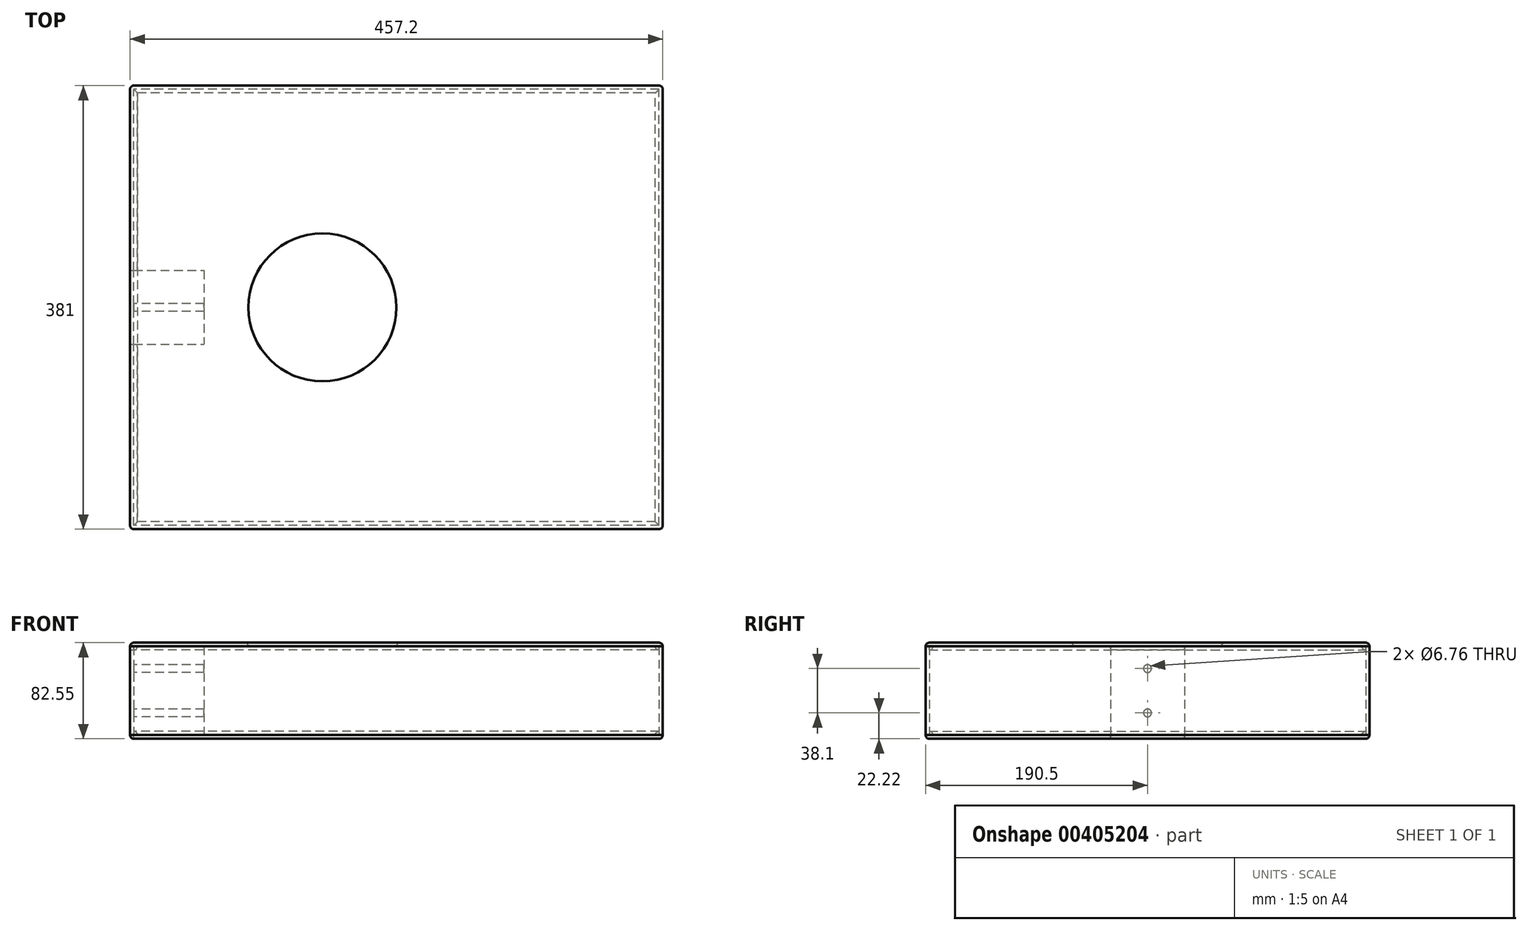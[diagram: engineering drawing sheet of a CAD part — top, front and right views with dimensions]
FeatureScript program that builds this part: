
annotation { "Feature Type Name" : "Feature", "Feature Type Description" : "" }
export const myFeature = defineFeature(function(context is Context, id is Id, definition is map)
    precondition{}
    {
        {
            var Q0;
            Q0=qCreatedBy(makeId("Top.planeOp"),FACE);
            var sketch = newSketch(context, id + "F0", { "sketchPlane" : qUnion([Q0])});
            skLineSegment(sketch, "E0.bottom", {"start": v(228.6, -190.5) * mm, "end": v(-228.6, -190.5) * mm});
            skLineSegment(sketch, "E0.top", {"start": v(228.6, 190.5) * mm, "end": v(-228.6, 190.5) * mm});
            skLineSegment(sketch, "E0.left", {"start": v(228.6, -190.5) * mm, "end": v(228.6, 190.5) * mm});
            skLineSegment(sketch, "E0.right", {"start": v(-228.6, -190.5) * mm, "end": v(-228.6, 190.5) * mm});
            skPoint(sketch, "E0.middle", {"position": v(0, 0) * mm});
            skLineSegment(sketch, "E1", {"start": v(-228.6, 0) * mm, "end": v(228.6, 0) * mm, "construction": true});
            skLineSegment(sketch, "E2.bottom", {"start": v(-228.6, 31.75) * mm, "end": v(-165.1, 31.75) * mm});
            skLineSegment(sketch, "E2.top", {"start": v(-228.6, -31.75) * mm, "end": v(-165.1, -31.75) * mm});
            skLineSegment(sketch, "E2.left", {"start": v(-228.6, 31.75) * mm, "end": v(-228.6, -31.75) * mm});
            skLineSegment(sketch, "E2.right", {"start": v(-165.1, 31.75) * mm, "end": v(-165.1, -31.75) * mm});
            skLineSegment(sketch, "E3.0", {"start": v(225.43, 187.33) * mm, "end": v(-225.43, 187.32) * mm});
            skLineSegment(sketch, "E3.1", {"start": v(225.43, -187.32) * mm, "end": v(225.42, 187.32) * mm});
            skLineSegment(sketch, "E3.2", {"start": v(225.43, -187.32) * mm, "end": v(-225.43, -187.33) * mm});
            skLineSegment(sketch, "E3.3", {"start": v(-225.42, -187.32) * mm, "end": v(-225.43, -31.75) * mm});
            skLineSegment(sketch, "E4.trimOffspring", {"start": v(-225.43, 31.75) * mm, "end": v(-225.43, 187.32) * mm});
            skLineSegment(sketch, "E5", {"start": v(-225.42, 187.32) * mm, "end": v(225.42, -187.32) * mm, "construction": true});
            skLineSegment(sketch, "E6", {"start": v(225.43, 187.33) * mm, "end": v(-225.43, -187.33) * mm, "construction": true});
            skLineSegment(sketch, "E7", {"start": v(-225.43, 109.54) * mm, "end": v(225.43, 109.54) * mm, "construction": true});
            skLineSegment(sketch, "E8", {"start": v(-225.42, -109.54) * mm, "end": v(225.42, -109.54) * mm, "construction": true});
            skLineSegment(sketch, "E9.0", {"start": v(-222.25, 31.75) * mm, "end": v(-222.25, 184.15) * mm});
            skLineSegment(sketch, "E9.1", {"start": v(-222.25, -184.15) * mm, "end": v(-222.25, -31.75) * mm});
            skLineSegment(sketch, "E9.2", {"start": v(222.25, -184.15) * mm, "end": v(-222.25, -184.15) * mm});
            skLineSegment(sketch, "E9.3", {"start": v(222.25, -184.15) * mm, "end": v(222.25, 184.15) * mm});
            skLineSegment(sketch, "E9.4", {"start": v(222.25, 184.15) * mm, "end": v(-222.25, 184.15) * mm});
            skLineSegment(sketch, "E10", {"start": v(-225.43, -31.75) * mm, "end": v(-225.43, 31.75) * mm});
            skSolve(sketch);
        }
        {
            var Q0;
            {var subQ9=sQuery(id+"F0.wireOp",EDGE,"E0.bottom");Q0=makeQuery(id+"F0.imprint","IMPRINT",FACE,{"disambiguationData":[TD([[makeQuery(id+"F0.imprint","IMPRINT",EDGE,{"derivedFrom":subQ9}),-1.0]])]});}
            var Q1;
            {var subQ0=sQuery(id+"F0.wireOp",EDGE,"E2.left");Q1=makeQuery(id+"F0.imprint","IMPRINT",FACE,{"disambiguationData":[TD([[makeQuery(id+"F0.imprint","IMPRINT",EDGE,{"derivedFrom":subQ0}),1.0]])]});}
            extrude(context, id + "F1", {"entities" : qUnion([Q0, Q1]), "depth" : 76.2 * mm});
        }
        {
            var Q0;
            Q0=makeQuery(id+"F0.imprint","IMPRINT",FACE,{"disambiguationData":[TD([[makeQuery(id+"F0.imprint","IMPRINT",EDGE,{"derivedFrom":sQuery(id+"F0.wireOp",EDGE,"E3.0")}),1.0]])]});
            extrude(context, id + "F2", {"entities" : qUnion([Q0]), "depth" : 3.17 * mm});
        }
        {
            var Q0;
            {var subQ0=sQuery(id+"F0.wireOp",EDGE,"E2.right");Q0=makeQuery(id+"F0.imprint","IMPRINT",FACE,{"disambiguationData":[TD([[makeQuery(id+"F0.imprint","IMPRINT",EDGE,{"derivedFrom":subQ0}),-1.0]])]});}
            extrude(context, id + "F3", {"entities" : qUnion([Q0]), "depth" : 76.2 * mm});
        }
        {
            var Q0;
            {var subQ22=sQuery(id+"F0.wireOp",EDGE,"E2.right");Q0=makeQuery(id+"F0.imprint","IMPRINT",FACE,{"disambiguationData":[TD([[makeQuery(id+"F0.imprint","IMPRINT",EDGE,{"derivedFrom":subQ22}),1.0]])]});}
            var Q1;
            {var subQ9=sQuery(id+"F0.wireOp",EDGE,"E0.bottom");Q1=makeQuery(id+"F0.imprint","IMPRINT",FACE,{"disambiguationData":[TD([[makeQuery(id+"F0.imprint","IMPRINT",EDGE,{"derivedFrom":subQ9}),-1.0]])]});}
            var Q2;
            Q2=makeQuery(id+"F0.imprint","IMPRINT",FACE,{"disambiguationData":[TD([[makeQuery(id+"F0.imprint","IMPRINT",EDGE,{"derivedFrom":sQuery(id+"F0.wireOp",EDGE,"E3.0")}),1.0]])]});
            var Q3;
            {var subQ3=sQuery(id+"F0.wireOp",EDGE,"9cd653e2-5831-4ef2-81ab-d4589cb25bf60.MirrorCS");var subQ5=sQuery(id+"F0.wireOp",EDGE,"FzasoPsy-j5LI-SKMa-pJql-VMQi0rBRJnUh");var subQ7=makeQuery(id+"F0.imprint","INTERSECT",VERTEX,{"derivedFrom":[subQ5,subQ3,sQuery(id+"F0.wireOp",EDGE,"aZBs2FEg-NMFi-UrqN-aLSZ-2lPHPGAGJXjl")]});Q3=makeQuery(id+"F0.imprint","IMPRINT",FACE,{"disambiguationData":[TD([[makeQuery(id+"F0.imprint","IMPRINT",EDGE,{"disambiguationData":[TD([[subQ7,-1.0]])],"derivedFrom":subQ5}),1.0]])]});}
            var Q4;
            {var subQ3=sQuery(id+"F0.wireOp",EDGE,"266a0d68-b8df-42f1-9db3-1c0c4b850da00.MirrorCS");var subQ5=sQuery(id+"F0.wireOp",EDGE,"953ce75e-d67b-4efc-bb00-0bf9153aae580.MirrorCS");var subQ6=makeQuery(id+"F0.imprint","INTERSECT",VERTEX,{"derivedFrom":[subQ5,subQ3]});Q4=makeQuery(id+"F0.imprint","IMPRINT",FACE,{"disambiguationData":[TD([[makeQuery(id+"F0.imprint","IMPRINT",EDGE,{"disambiguationData":[TD([[subQ6,-1.0]])],"derivedFrom":subQ5}),-1.0]])]});}
            var Q5;
            {var subQ0=sQuery(id+"F0.wireOp",EDGE,"htOpjW4I-LsWA-SOcr-SaNu-1bdWkilzWaC8");Q5=makeQuery(id+"F0.imprint","IMPRINT",FACE,{"disambiguationData":[TD([[makeQuery(id+"F0.imprint","IMPRINT",EDGE,{"derivedFrom":subQ0}),1.0]])]});}
            var Q6;
            {var subQ0=sQuery(id+"F0.wireOp",EDGE,"Kqx6j9Af-swEe-v3Xz-Lvxc-ByTmGhM5A1qr");Q6=makeQuery(id+"F0.imprint","IMPRINT",FACE,{"disambiguationData":[TD([[makeQuery(id+"F0.imprint","IMPRINT",EDGE,{"derivedFrom":subQ0}),-1.0]])]});}
            var Q7;
            {var subQ0=sQuery(id+"F0.wireOp",EDGE,"BsV5Qlrn-ofVC-NWyB-0alZ-GxZEvTZdQiUt");Q7=makeQuery(id+"F0.imprint","IMPRINT",FACE,{"disambiguationData":[TD([[makeQuery(id+"F0.imprint","IMPRINT",EDGE,{"derivedFrom":subQ0}),1.0]])]});}
            var Q8;
            {var subQ0=sQuery(id+"F0.wireOp",EDGE,"MGyNNtHl-DI8I-UvPv-GyAB-l8y68qR5pJX8");Q8=makeQuery(id+"F0.imprint","IMPRINT",FACE,{"disambiguationData":[TD([[makeQuery(id+"F0.imprint","IMPRINT",EDGE,{"derivedFrom":subQ0}),1.0]])]});}
            var Q9;
            {var subQ3=sQuery(id+"F0.wireOp",EDGE,"Kqx6j9Af-swEe-v3Xz-Lvxc-ByTmGhM5A1qr");Q9=makeQuery(id+"F0.imprint","IMPRINT",FACE,{"disambiguationData":[TD([[makeQuery(id+"F0.imprint","IMPRINT",EDGE,{"derivedFrom":subQ3}),1.0]])]});}
            var Q10;
            {var subQ2=sQuery(id+"F0.wireOp",EDGE,"2eb42779-513d-4441-a8d7-d657dc6821a70.MirrorCS");Q10=makeQuery(id+"F0.imprint","IMPRINT",FACE,{"disambiguationData":[TD([[makeQuery(id+"F0.imprint","IMPRINT",EDGE,{"derivedFrom":subQ2}),-1.0]])]});}
            var Q11;
            {var subQ0=sQuery(id+"F0.wireOp",EDGE,"953ce75e-d67b-4efc-bb00-0bf9153aae580.MirrorCS");var subQ1=sQuery(id+"F0.wireOp",EDGE,"9e805463-2b13-41b5-8116-62ebd402cd080.MirrorCS");var subQ2=makeQuery(id+"F0.imprint","INTERSECT",VERTEX,{"derivedFrom":[subQ1,subQ0]});Q11=makeQuery(id+"F0.imprint","IMPRINT",FACE,{"disambiguationData":[TD([[makeQuery(id+"F0.imprint","IMPRINT",EDGE,{"disambiguationData":[TD([[subQ2,1.0]])],"derivedFrom":subQ0}),-1.0]])]});}
            var Q12;
            {var subQ0=sQuery(id+"F0.wireOp",EDGE,"GMDVnvmZ-OlzJ-OGz9-7dtt-hA1VzcQCeQrP");var subQ1=sQuery(id+"F0.wireOp",EDGE,"1a1ql4DQ-ibnV-jcih-jIlv-f0bGRyVOqIzY");var subQ2=makeQuery(id+"F0.imprint","INTERSECT",VERTEX,{"derivedFrom":[subQ1,subQ0]});Q12=makeQuery(id+"F0.imprint","IMPRINT",FACE,{"disambiguationData":[TD([[makeQuery(id+"F0.imprint","IMPRINT",EDGE,{"disambiguationData":[TD([[subQ2,-1.0]])],"derivedFrom":subQ0}),1.0]])]});}
            var Q13;
            {var subQ0=sQuery(id+"F0.wireOp",EDGE,"953ce75e-d67b-4efc-bb00-0bf9153aae580.MirrorCS");var subQ1=sQuery(id+"F0.wireOp",EDGE,"9cd653e2-5831-4ef2-81ab-d4589cb25bf60.MirrorCS");var subQ2=makeQuery(id+"F0.imprint","INTERSECT",VERTEX,{"derivedFrom":[subQ1,subQ0]});Q13=makeQuery(id+"F0.imprint","IMPRINT",FACE,{"disambiguationData":[TD([[makeQuery(id+"F0.imprint","IMPRINT",EDGE,{"disambiguationData":[TD([[subQ2,-1.0]])],"derivedFrom":subQ0}),-1.0]])]});}
            var Q14;
            {var subQ0=sQuery(id+"F0.wireOp",EDGE,"FzasoPsy-j5LI-SKMa-pJql-VMQi0rBRJnUh");var subQ1=sQuery(id+"F0.wireOp",EDGE,"GMDVnvmZ-OlzJ-OGz9-7dtt-hA1VzcQCeQrP");var subQ2=makeQuery(id+"F0.imprint","INTERSECT",VERTEX,{"derivedFrom":[subQ1,subQ0]});Q14=makeQuery(id+"F0.imprint","IMPRINT",FACE,{"disambiguationData":[TD([[makeQuery(id+"F0.imprint","IMPRINT",EDGE,{"disambiguationData":[TD([[subQ2,1.0]])],"derivedFrom":subQ1}),1.0]])]});}
            var Q15;
            {var subQ0=sQuery(id+"F0.wireOp",EDGE,"E2.left");Q15=makeQuery(id+"F0.imprint","IMPRINT",FACE,{"disambiguationData":[TD([[makeQuery(id+"F0.imprint","IMPRINT",EDGE,{"derivedFrom":subQ0}),1.0]])]});}
            var Q16;
            Q16=makeQuery(id+"F0.imprint","IMPRINT",FACE,{"disambiguationData":[TD([[makeQuery(id+"F0.imprint","IMPRINT",EDGE,{"derivedFrom":sQuery(id+"F0.wireOp",EDGE,"4894fb85-a18e-4dc9-a42a-9e5500fa191a0.MirrorCS")}),1.0]])]});
            var Q17;
            {var subQ0=sQuery(id+"F0.wireOp",EDGE,"E2.right");Q17=makeQuery(id+"F0.imprint","IMPRINT",FACE,{"disambiguationData":[TD([[makeQuery(id+"F0.imprint","IMPRINT",EDGE,{"derivedFrom":subQ0}),-1.0]])]});}
            extrude(context, id + "F4", {"entities" : qUnion([Q0, Q1, Q2, Q3, Q4, Q5, Q6, Q7, Q8, Q9, Q10, Q11, Q12, Q13, Q14, Q15, Q16, Q17]), "oppositeDirection" : true, "depth" : 3.17 * mm});
        }
        {
            var Q0;
            Q0=makeQuery(id+"F2.opExtrude","CAP_EDGE",EDGE,{"disambiguationData":[OSD([sQuery(id+"F0.wireOp",EDGE,"E9.0")])],"isStart":false});
            var Q1;
            Q1=makeQuery(id+"F2.opExtrude","CAP_EDGE",EDGE,{"disambiguationData":[OSD([sQuery(id+"F0.wireOp",EDGE,"E9.4")])],"isStart":false});
            var Q2;
            Q2=makeQuery(id+"F2.opExtrude","CAP_EDGE",EDGE,{"disambiguationData":[OSD([sQuery(id+"F0.wireOp",EDGE,"E9.1")])],"isStart":false});
            var Q3;
            Q3=makeQuery(id+"F2.opExtrude","CAP_EDGE",EDGE,{"disambiguationData":[OSD([sQuery(id+"F0.wireOp",EDGE,"E9.2")])],"isStart":false});
            var Q4;
            Q4=makeQuery(id+"F2.opExtrude","CAP_EDGE",EDGE,{"disambiguationData":[OSD([sQuery(id+"F0.wireOp",EDGE,"E9.3")])],"isStart":false});
            fillet(context, id + "F5", {"entities" : qUnion([Q0, Q1, Q2, Q3, Q4]), "radius" : 3.17 * mm, "tangentPropagation" : true, "allowEdgeOverflow" : false});
        }
        {
            var Q0;
            {var subQ0=sQuery(id+"F0.wireOp",EDGE,"E0.right");var subQ1=sQuery(id+"F0.wireOp",EDGE,"E0.top");Q0=makeQuery(id+"F4.boolean.opBoolean","MERGE",EDGE,{"derivedFrom":[makeQuery(id+"F1.opExtrude","SWEPT_EDGE",EDGE,{"disambiguationData":[OSD([subQ1,subQ0])]}),makeQuery(id+"F4.opExtrude","SWEPT_EDGE",EDGE,{"disambiguationData":[OSD([subQ1,subQ0])]})]});}
            var Q1;
            {var subQ0=sQuery(id+"F0.wireOp",EDGE,"E0.left");var subQ1=sQuery(id+"F0.wireOp",EDGE,"E0.top");Q1=makeQuery(id+"F4.boolean.opBoolean","MERGE",EDGE,{"derivedFrom":[makeQuery(id+"F1.opExtrude","SWEPT_EDGE",EDGE,{"disambiguationData":[OSD([subQ1,subQ0])]}),makeQuery(id+"F4.opExtrude","SWEPT_EDGE",EDGE,{"disambiguationData":[OSD([subQ1,subQ0])]})]});}
            var Q2;
            {var subQ0=sQuery(id+"F0.wireOp",EDGE,"E0.right");var subQ1=sQuery(id+"F0.wireOp",EDGE,"E0.bottom");Q2=makeQuery(id+"F4.boolean.opBoolean","MERGE",EDGE,{"derivedFrom":[makeQuery(id+"F1.opExtrude","SWEPT_EDGE",EDGE,{"disambiguationData":[OSD([subQ1,subQ0])]}),makeQuery(id+"F4.opExtrude","SWEPT_EDGE",EDGE,{"disambiguationData":[OSD([subQ1,subQ0])]})]});}
            var Q3;
            {var subQ0=sQuery(id+"F0.wireOp",EDGE,"E0.left");var subQ1=sQuery(id+"F0.wireOp",EDGE,"E0.bottom");Q3=makeQuery(id+"F4.boolean.opBoolean","MERGE",EDGE,{"derivedFrom":[makeQuery(id+"F1.opExtrude","SWEPT_EDGE",EDGE,{"disambiguationData":[OSD([subQ1,subQ0])]}),makeQuery(id+"F4.opExtrude","SWEPT_EDGE",EDGE,{"disambiguationData":[OSD([subQ1,subQ0])]})]});}
            var Q4;
            Q4=makeQuery(id+"F4.opExtrude","CAP_EDGE",EDGE,{"disambiguationData":[OSD([sQuery(id+"F0.wireOp",EDGE,"E0.bottom")])],"isStart":false});
            var Q5;
            Q5=makeQuery(id+"F4.opExtrude","CAP_EDGE",EDGE,{"disambiguationData":[OSD([sQuery(id+"F0.wireOp",EDGE,"E0.left")])],"isStart":false});
            var Q6;
            Q6=makeQuery(id+"F4.opExtrude","CAP_EDGE",EDGE,{"disambiguationData":[OSD([sQuery(id+"F0.wireOp",EDGE,"E0.top")])],"isStart":false});
            var Q7;
            Q7=makeQuery(id+"F4.opExtrude","CAP_EDGE",EDGE,{"disambiguationData":[OSD([sQuery(id+"F0.wireOp",EDGE,"E0.right"),sQuery(id+"F0.wireOp",EDGE,"E2.left")])],"isStart":false});
            fillet(context, id + "F6", {"entities" : qUnion([Q0, Q1, Q2, Q3, Q4, Q5, Q6, Q7]), "radius" : 3.17 * mm, "tangentPropagation" : true, "allowEdgeOverflow" : false});
        }
        {
            var Q0;
            Q0=makeQuery(id+"F1.opExtrude","CAP_FACE",FACE,{"disambiguationData":[OSD([sQuery(id+"F0.wireOp",EDGE,"E0.bottom"),sQuery(id+"F0.wireOp",EDGE,"E0.top"),sQuery(id+"F0.wireOp",EDGE,"E0.left"),sQuery(id+"F0.wireOp",EDGE,"E0.right"),sQuery(id+"F0.wireOp",EDGE,"E2.bottom"),sQuery(id+"F0.wireOp",EDGE,"E2.top"),sQuery(id+"F0.wireOp",EDGE,"E3.0"),sQuery(id+"F0.wireOp",EDGE,"E3.1"),sQuery(id+"F0.wireOp",EDGE,"E3.2"),sQuery(id+"F0.wireOp",EDGE,"E3.3"),sQuery(id+"F0.wireOp",EDGE,"E4.trimOffspring")])],"isStart":false});
            var sketch = newSketch(context, id + "F7", { "sketchPlane" : qUnion([Q0])});
            skLineSegment(sketch, "E11.bottom", {"start": v(-228.6, 190.5) * mm, "end": v(228.6, 190.5) * mm});
            skLineSegment(sketch, "E11.top", {"start": v(-228.6, -190.5) * mm, "end": v(228.6, -190.5) * mm});
            skLineSegment(sketch, "E11.left", {"start": v(-228.6, 190.5) * mm, "end": v(-228.6, -190.5) * mm});
            skLineSegment(sketch, "E11.right", {"start": v(228.6, 190.5) * mm, "end": v(228.6, -190.5) * mm});
            skLineSegment(sketch, "E12", {"start": v(0, 0) * mm, "end": v(-63.5, 0) * mm, "construction": true});
            skCircle(sketch, "E13", {"center": v(-63.5, 0) * mm, "radius": 63.5 * mm});
            skLineSegment(sketch, "E14.0", {"start": v(222.25, 184.15) * mm, "end": v(222.25, -184.15) * mm});
            skLineSegment(sketch, "E14.1", {"start": v(-222.25, 184.15) * mm, "end": v(222.25, 184.15) * mm});
            skLineSegment(sketch, "E14.2", {"start": v(-222.25, 184.15) * mm, "end": v(-222.25, -184.15) * mm});
            skLineSegment(sketch, "E14.3", {"start": v(-222.25, -184.15) * mm, "end": v(222.25, -184.15) * mm});
            skSolve(sketch);
        }
        {
            var Q0;
            Q0=makeQuery(id+"F7.imprint","IMPRINT",FACE,{"disambiguationData":[TD([[makeQuery(id+"F7.imprint","IMPRINT",EDGE,{"derivedFrom":sQuery(id+"F7.wireOp",EDGE,"E14.0")}),1.0]])]});
            extrude(context, id + "F8", {"entities" : qUnion([Q0]), "oppositeDirection" : true, "depth" : 3.17 * mm});
        }
        {
            var Q0;
            Q0=makeQuery(id+"F8.opExtrude","CAP_EDGE",EDGE,{"disambiguationData":[OSD([sQuery(id+"F7.wireOp",EDGE,"E14.0")])],"isStart":false});
            var Q1;
            Q1=makeQuery(id+"F8.opExtrude","CAP_EDGE",EDGE,{"disambiguationData":[OSD([sQuery(id+"F7.wireOp",EDGE,"E14.3")])],"isStart":false});
            var Q2;
            Q2=makeQuery(id+"F8.opExtrude","CAP_EDGE",EDGE,{"disambiguationData":[OSD([sQuery(id+"F7.wireOp",EDGE,"E14.2")])],"isStart":false});
            var Q3;
            Q3=makeQuery(id+"F8.opExtrude","CAP_EDGE",EDGE,{"disambiguationData":[OSD([sQuery(id+"F7.wireOp",EDGE,"E14.1")])],"isStart":false});
            fillet(context, id + "F9", {"entities" : qUnion([Q0, Q1, Q2, Q3]), "radius" : 3.17 * mm, "tangentPropagation" : true, "allowEdgeOverflow" : false});
        }
        {
            var Q0;
            {var subQ5=sQuery(id+"F0.wireOp",EDGE,"E3.0");Q0=makeQuery(id+"F7.imprint","IMPRINT",FACE,{"disambiguationData":[TD([[makeQuery(id+"F7.imprint","IMPRINT",EDGE,{"derivedFrom":makeQuery(id+"F1.opExtrude","CAP_EDGE",EDGE,{"disambiguationData":[OSD([subQ5])],"isStart":false})}),-1.0]])]});}
            var Q1;
            Q1=makeQuery(id+"F7.imprint","IMPRINT",FACE,{"disambiguationData":[TD([[makeQuery(id+"F7.imprint","IMPRINT",EDGE,{"derivedFrom":sQuery(id+"F7.wireOp",EDGE,"E14.0")}),1.0]])]});
            var Q2;
            Q2=makeQuery(id+"F7.imprint","IMPRINT",FACE,{"disambiguationData":[TD([[makeQuery(id+"F7.imprint","IMPRINT",EDGE,{"derivedFrom":sQuery(id+"F7.wireOp",EDGE,"E13")}),-1.0]])]});
            extrude(context, id + "F10", {"entities" : qUnion([Q0, Q1, Q2]), "depth" : 3.17 * mm});
        }
        {
            var Q0;
            Q0=makeQuery(id+"F10.opExtrude","CAP_EDGE",EDGE,{"disambiguationData":[OSD([sQuery(id+"F7.wireOp",EDGE,"E11.right")])],"isStart":false});
            var Q1;
            Q1=makeQuery(id+"F10.opExtrude","CAP_EDGE",EDGE,{"disambiguationData":[OSD([sQuery(id+"F7.wireOp",EDGE,"E13")])],"isStart":false});
            fillet(context, id + "F11", {"entities" : qUnion([Q0, Q1]), "radius" : 3.17 * mm, "tangentPropagation" : true, "allowEdgeOverflow" : false});
        }
        {
            var Q0;
            Q0=makeQuery(id+"F1.opExtrude","SWEPT_FACE",FACE,{"disambiguationData":[OSD([sQuery(id+"F0.wireOp",EDGE,"E0.right"),sQuery(id+"F0.wireOp",EDGE,"E2.left")])]});
            var sketch = newSketch(context, id + "F12", { "sketchPlane" : qUnion([Q0])});
            skLineSegment(sketch, "E15", {"start": v(0, 0) * mm, "end": v(0, 76.2) * mm, "construction": true});
            skLineSegment(sketch, "E16", {"start": v(0, 76.2) * mm, "end": v(0, 57.15) * mm, "construction": true});
            skLineSegment(sketch, "E17", {"start": v(0, 0) * mm, "end": v(0, 19.05) * mm, "construction": true});
            skSolve(sketch);
        }
        {
            var Q0;
            Q0=sQuery(id+"F12.wireOp",VERTEX,"E16.end");
            var Q1;
            Q1=sQuery(id+"F12.wireOp",VERTEX,"E17.end");
            var Q2;
            Q2=makeQuery(id+"F1.opExtrude","SWEPT_BODY",BODY,{"disambiguationData":[OSD([sQuery(id+"F0.wireOp",EDGE,"E0.bottom"),sQuery(id+"F0.wireOp",EDGE,"E0.top"),sQuery(id+"F0.wireOp",EDGE,"E0.left"),sQuery(id+"F0.wireOp",EDGE,"E0.right"),sQuery(id+"F0.wireOp",EDGE,"E2.left"),sQuery(id+"F0.wireOp",EDGE,"E3.0"),sQuery(id+"F0.wireOp",EDGE,"E3.1"),sQuery(id+"F0.wireOp",EDGE,"E3.2"),sQuery(id+"F0.wireOp",EDGE,"E3.3"),sQuery(id+"F0.wireOp",EDGE,"E4.trimOffspring"),sQuery(id+"F0.wireOp",EDGE,"E10")])]});
            var Q3;
            Q3=makeQuery(id+"F3.opExtrude","SWEPT_BODY",BODY,{"disambiguationData":[OSD([sQuery(id+"F0.wireOp",EDGE,"E2.bottom"),sQuery(id+"F0.wireOp",EDGE,"E2.top"),sQuery(id+"F0.wireOp",EDGE,"E2.right"),sQuery(id+"F0.wireOp",EDGE,"E10")])]});
            hole(context, id + "F13", {"style" : HoleStyle.SIMPLE, "endStyle" : HoleEndStyle.BLIND, "standardTappedOrClearance" : lookupTablePath({ "standard" : "ANSI", "fit" : "Normal (ASME)", "size" : "1/4", "type" : "Clearance" }), "standardBlindInLast" : lookupTablePath({ "fit" : "Free", "standard" : "ANSI", "size" : "1/4", "type" : "Clearance" }), "holeDiameter" : 6.76 * mm, "holeDepth" : 63.5 * mm, "isTappedThrough" : true, "tappedDepth" : 12.7 * mm, "tapClearance" : 3, "locations" : qUnion([Q0, Q1]), "scope" : qUnion([Q2, Q3])});
        }
    });
